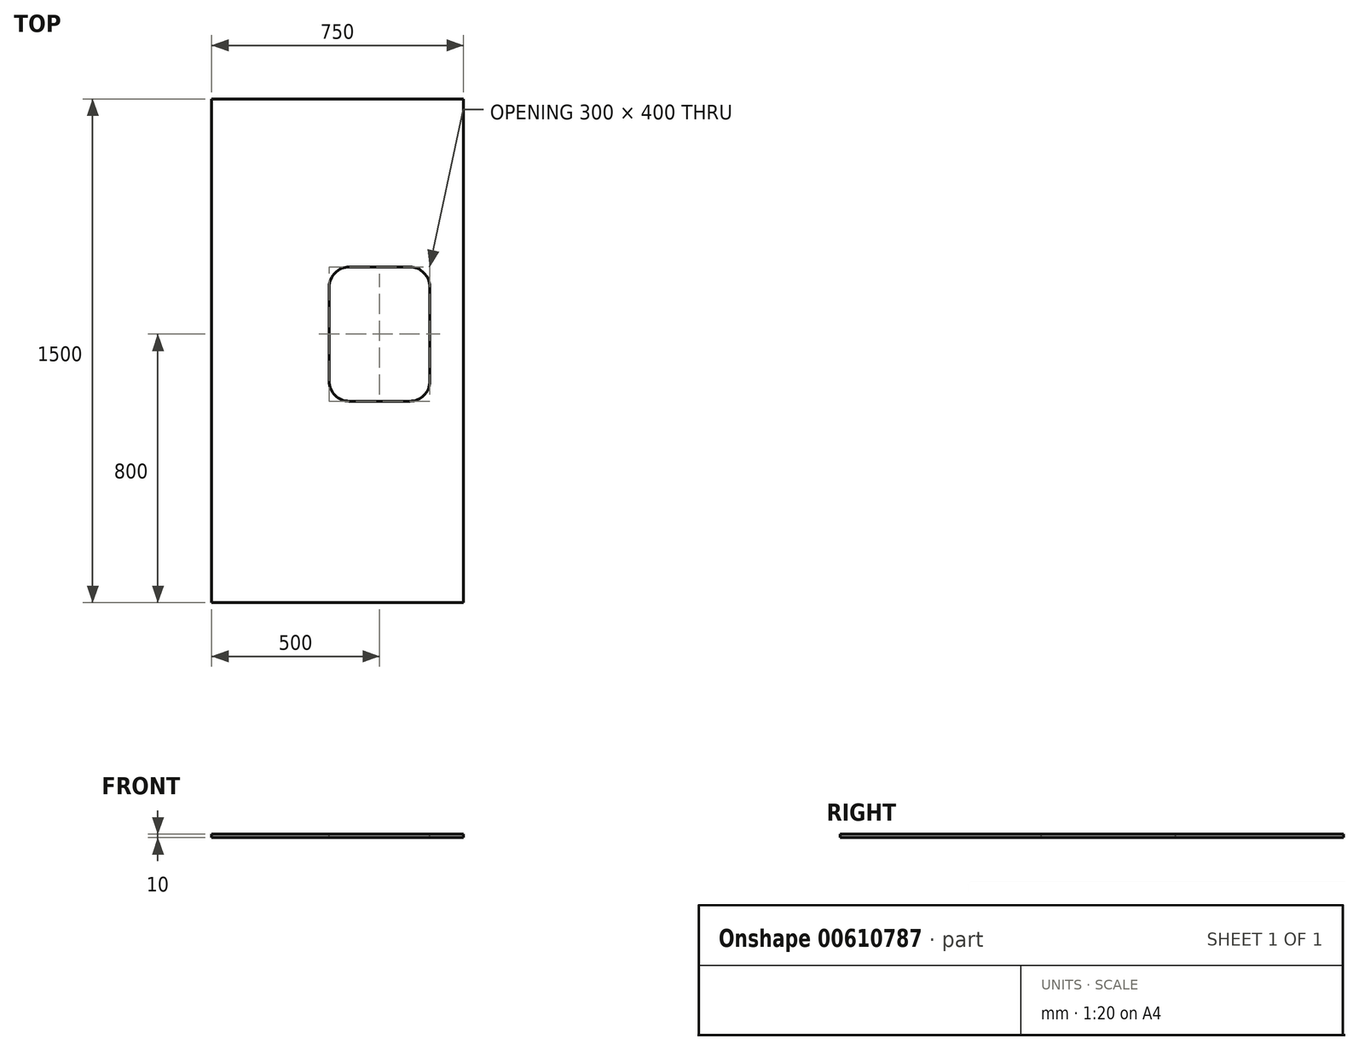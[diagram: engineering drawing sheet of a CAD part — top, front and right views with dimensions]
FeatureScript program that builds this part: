
annotation { "Feature Type Name" : "Feature", "Feature Type Description" : "" }
export const myFeature = defineFeature(function(context is Context, id is Id, definition is map)
    precondition{}
    {
        {
            var Q0;
            Q0=qCreatedBy(makeId("Top.planeOp"),FACE);
            var sketch = newSketch(context, id + "F0", { "sketchPlane" : qUnion([Q0])});
            skLineSegment(sketch, "E0.bottom", {"start": v(-750, 1100) * mm, "end": v(0, 1100) * mm});
            skLineSegment(sketch, "E0.top", {"start": v(-750, 0) * mm, "end": v(0, 0) * mm});
            skLineSegment(sketch, "E0.left", {"start": v(0, 1100) * mm, "end": v(0, 0) * mm});
            skLineSegment(sketch, "E0.right", {"start": v(-750, 1100) * mm, "end": v(-750, 0) * mm});
            skSolve(sketch);
        }
        {
            var Q0;
            Q0 = qSketchRegion(id + "F0", true);
            extrude(context, id + "F1", {"entities" : qUnion([Q0]), "depth" : 10 * mm, "offsetDistance" : 25 * mm});
        }
        {
            var Q0;
            Q0=makeQuery(id+"F1.opExtrude","CAP_FACE",FACE,{"disambiguationData":[OSD([sQuery(id+"F0.wireOp",EDGE,"E0.bottom"),sQuery(id+"F0.wireOp",EDGE,"E0.top"),sQuery(id+"F0.wireOp",EDGE,"E0.left"),sQuery(id+"F0.wireOp",EDGE,"E0.right")])],"isStart":false});
            var sketch = newSketch(context, id + "F2", { "sketchPlane" : qUnion([Q0])});
            skLineSegment(sketch, "E1.bottom", {"start": v(-750, 1100) * mm, "end": v(0, 1100) * mm});
            skLineSegment(sketch, "E1.top", {"start": v(-750, 1500) * mm, "end": v(0, 1500) * mm});
            skLineSegment(sketch, "E1.left", {"start": v(0, 1500) * mm, "end": v(0, 1100) * mm});
            skLineSegment(sketch, "E1.right", {"start": v(-750, 1500) * mm, "end": v(-750, 1100) * mm});
            skSolve(sketch);
        }
        {
            var Q0;
            Q0=makeQuery(id+"F2.imprint","IMPRINT",FACE,{"disambiguationData":[TD([[makeQuery(id+"F2.imprint","IMPRINT",EDGE,{"derivedFrom":sQuery(id+"F2.wireOp",EDGE,"E1.bottom")}),1.0]])]});
            extrude(context, id + "F3", {"entities" : qUnion([Q0]), "operationType" : NewBodyOperationType.ADD, "oppositeDirection" : true, "depth" : 10 * mm, "offsetDistance" : 25 * mm});
        }
        {
            var Q0;
            Q0=makeQuery(id+"F3.boolean.opBoolean","MERGE",FACE,{"derivedFrom":[makeQuery(id+"F1.opExtrude","CAP_FACE",FACE,{"disambiguationData":[OSD([sQuery(id+"F0.wireOp",EDGE,"E0.bottom"),sQuery(id+"F0.wireOp",EDGE,"E0.top"),sQuery(id+"F0.wireOp",EDGE,"E0.left"),sQuery(id+"F0.wireOp",EDGE,"E0.right")])],"isStart":false}),makeQuery(id+"F3.opExtrude","CAP_FACE",FACE,{"disambiguationData":[OSD([sQuery(id+"F2.wireOp",EDGE,"E1.bottom"),sQuery(id+"F2.wireOp",EDGE,"E1.top"),sQuery(id+"F2.wireOp",EDGE,"E1.left"),sQuery(id+"F2.wireOp",EDGE,"E1.right")])],"isStart":true})]});
            var sketch = newSketch(context, id + "F4", { "sketchPlane" : qUnion([Q0])});
            skLineSegment(sketch, "E2.bottom", {"start": v(-100, 600) * mm, "end": v(-400, 600) * mm});
            skLineSegment(sketch, "E2.top", {"start": v(-100, 1000) * mm, "end": v(-400, 1000) * mm});
            skLineSegment(sketch, "E2.left", {"start": v(-100, 600) * mm, "end": v(-100, 1000) * mm});
            skLineSegment(sketch, "E2.right", {"start": v(-400, 600) * mm, "end": v(-400, 1000) * mm});
            skSolve(sketch);
        }
        {
            var Q0;
            Q0=makeQuery(id+"F4.imprint","IMPRINT",FACE,{"disambiguationData":[TD([[makeQuery(id+"F4.imprint","IMPRINT",EDGE,{"derivedFrom":sQuery(id+"F4.wireOp",EDGE,"E2.bottom")}),-1.0]])]});
            extrude(context, id + "F5", {"entities" : qUnion([Q0]), "operationType" : NewBodyOperationType.REMOVE, "oppositeDirection" : true, "depth" : 25 * mm, "offsetDistance" : 25 * mm});
        }
        {
            var Q0;
            Q0=makeQuery(id+"F5.boolean.opBoolean","COPY",EDGE,{"derivedFrom":makeQuery(id+"F5.opExtrude","SWEPT_EDGE",EDGE,{"disambiguationData":[OSD([sQuery(id+"F4.wireOp",EDGE,"E2.top"),sQuery(id+"F4.wireOp",EDGE,"E2.right")])]})});
            var Q1;
            Q1=makeQuery(id+"F5.boolean.opBoolean","COPY",EDGE,{"derivedFrom":makeQuery(id+"F5.opExtrude","SWEPT_EDGE",EDGE,{"disambiguationData":[OSD([sQuery(id+"F4.wireOp",EDGE,"E2.bottom"),sQuery(id+"F4.wireOp",EDGE,"E2.right")])]})});
            var Q2;
            Q2=makeQuery(id+"F5.boolean.opBoolean","COPY",EDGE,{"derivedFrom":makeQuery(id+"F5.opExtrude","SWEPT_EDGE",EDGE,{"disambiguationData":[OSD([sQuery(id+"F4.wireOp",EDGE,"E2.top"),sQuery(id+"F4.wireOp",EDGE,"E2.left")])]})});
            var Q3;
            Q3=makeQuery(id+"F5.boolean.opBoolean","COPY",EDGE,{"derivedFrom":makeQuery(id+"F5.opExtrude","SWEPT_EDGE",EDGE,{"disambiguationData":[OSD([sQuery(id+"F4.wireOp",EDGE,"E2.bottom"),sQuery(id+"F4.wireOp",EDGE,"E2.left")])]})});
            fillet(context, id + "F6", {"entities" : qUnion([Q0, Q1, Q2, Q3]), "radius" : 60 * mm, "tangentPropagation" : true, "allowEdgeOverflow" : false});
        }
    });
